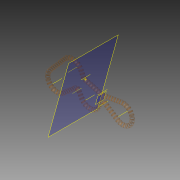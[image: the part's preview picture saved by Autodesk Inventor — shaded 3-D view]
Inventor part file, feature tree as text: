
AUTODESK INVENTOR PART (.ipt)
format: ipt  version: 2014 SP1 (Build 180222100, 222)  size: 463,360 bytes
history: native  units: mm (DEFAULTED — no unit token found)
features: other x96, extrude x86, sketch x2, plane x1, pattern_linear x1
ambient origin geometry x8: Origin, YZ Plane, XZ Plane, XY Plane, X Axis, Y Axis, Z Axis, Center Point
bodies: Body1 (feature_tree), Body2 (feature_tree), Body3 (feature_tree), Body4 (feature_tree), Body5 (feature_tree), Body6 (feature_tree), Body7 (feature_tree), Body8 (feature_tree), Body9 (feature_tree), Body10 (feature_tree), Body11 (feature_tree), Body12 (feature_tree), Body13 (feature_tree), Body14 (feature_tree), Body15 (feature_tree), Body16 (feature_tree), Body17 (feature_tree), Body18 (feature_tree), Body19 (feature_tree), Body20 (feature_tree), Body21 (feature_tree), Body22 (feature_tree), Body23 (feature_tree), Body24 (feature_tree), Body25 (feature_tree), Body26 (feature_tree), Body27 (feature_tree), Body28 (feature_tree), Body29 (feature_tree), Body30 (feature_tree), Body31 (feature_tree), Body32 (feature_tree), Body33 (feature_tree), Body34 (feature_tree), Body35 (feature_tree), Body36 (feature_tree), Body37 (feature_tree), Body38 (feature_tree), Body39 (feature_tree), Body40 (feature_tree), Body41 (feature_tree), Body42 (feature_tree), Body43 (feature_tree), Body44 (feature_tree), Body45 (feature_tree), Body46 (feature_tree), Body47 (feature_tree), Body48 (feature_tree), Body49 (feature_tree), Body50 (feature_tree), Body51 (feature_tree), Body52 (feature_tree), Body53 (feature_tree), Body54 (feature_tree), Body55 (feature_tree), Body56 (feature_tree), Body57 (feature_tree), Body58 (feature_tree), Body59 (feature_tree), Body60 (feature_tree), Body61 (feature_tree), Body62 (feature_tree), Body63 (feature_tree), Body64 (feature_tree), Body65 (feature_tree), Body66 (feature_tree), Body67 (feature_tree), Body68 (feature_tree), Body69 (feature_tree), Body70 (feature_tree), Body71 (feature_tree), Body72 (feature_tree), Body73 (feature_tree), Body74 (feature_tree), Body75 (feature_tree), Body76 (feature_tree), Body77 (feature_tree), Body78 (feature_tree), Body79 (feature_tree), Body80 (feature_tree), Body81 (feature_tree), Body82 (feature_tree), Body83 (feature_tree), Body84 (feature_tree), Body85 (feature_tree), Body86 (feature_tree)
feature tree (186):
  sketch  "Sketch Path"  dims[d7=0.0mm d8=0.0mm d9=0.0mm d10=0.0mm d11=0.0mm d12=0.0mm d13=0.0mm d14=0.0mm d15=0.0mm d16=5.08mm d17=0.0mm d18=860.0mm]
  other  "Cross Section Plane"
  other  "Work Axis1"
  other  "Work Axis2"
  other  "Work Axis3"
  other  "Work Axis4"
  other  "Work Axis5"
  other  "Work Axis6"
  other  "Work Axis7"
  other  "Work Axis8"
  other  "Work Point1"
  plane  "Work Plane2"
  pattern_linear  "Rectangular Pattern1"  Spacing1=5.08mm  [1 undecoded]
  sketch  "Sketch3"  dims[d0=0.0mm]
  other  "Srf1"
  other  "Srf2"
  other  "Srf3"
  other  "Srf4"
  other  "Srf5"
  other  "Srf6"
  other  "Srf7"
  other  "Srf8"
  other  "Srf9"
  other  "Srf10"
  other  "Srf11"
  other  "Srf12"
  other  "Srf13"
  other  "Srf14"
  other  "Srf15"
  other  "Srf16"
  other  "Srf17"
  other  "Srf18"
  other  "Srf19"
  other  "Srf20"
  other  "Srf21"
  other  "Srf22"
  other  "Srf23"
  other  "Srf24"
  other  "Srf25"
  other  "Srf26"
  other  "Srf27"
  other  "Srf28"
  other  "Srf29"
  other  "Srf30"
  other  "Srf31"
  other  "Srf32"
  other  "Srf33"
  other  "Srf34"
  other  "Srf35"
  other  "Srf36"
  other  "Srf37"
  other  "Srf38"
  other  "Srf39"
  other  "Srf40"
  other  "Srf41"
  other  "Srf42"
  other  "Srf43"
  other  "Srf44"
  other  "Srf45"
  other  "Srf46"
  other  "Srf47"
  other  "Srf48"
  other  "Srf49"
  other  "Srf50"
  other  "Srf51"
  other  "Srf52"
  other  "Srf53"
  other  "Srf54"
  other  "Srf55"
  other  "Srf56"
  other  "Srf57"
  other  "Srf58"
  other  "Srf59"
  other  "Srf60"
  other  "Srf61"
  other  "Srf62"
  other  "Srf63"
  other  "Srf64"
  other  "Srf65"
  other  "Srf66"
  other  "Srf67"
  other  "Srf68"
  other  "Srf69"
  other  "Srf70"
  other  "Srf71"
  other  "Srf72"
  other  "Srf73"
  other  "Srf74"
  other  "Srf75"
  other  "Srf76"
  other  "Srf77"
  other  "Srf78"
  other  "Srf79"
  other  "Srf80"
  other  "Srf81"
  other  "Srf82"
  other  "Srf83"
  other  "Srf84"
  other  "Srf85"
  other  "Srf86"
  extrude  "ExtrusionSrf1"  Depth=860.0mm
  extrude  "ExtrusionSrf2"  [1 undecoded]
  extrude  "ExtrusionSrf3"  [1 undecoded]
  extrude  "ExtrusionSrf4"  [1 undecoded]
  extrude  "ExtrusionSrf5"  [1 undecoded]
  extrude  "ExtrusionSrf6"  [1 undecoded]
  extrude  "ExtrusionSrf7"  [1 undecoded]
  extrude  "ExtrusionSrf8"  [1 undecoded]
  extrude  "ExtrusionSrf9"  [1 undecoded]
  extrude  "ExtrusionSrf10"  [1 undecoded]
  extrude  "ExtrusionSrf11"  [1 undecoded]
  extrude  "ExtrusionSrf12"  [1 undecoded]
  extrude  "ExtrusionSrf13"  [1 undecoded]
  extrude  "ExtrusionSrf14"  [1 undecoded]
  extrude  "ExtrusionSrf15"  [1 undecoded]
  extrude  "ExtrusionSrf16"  [1 undecoded]
  extrude  "ExtrusionSrf17"  [1 undecoded]
  extrude  "ExtrusionSrf18"  [1 undecoded]
  extrude  "ExtrusionSrf19"  [1 undecoded]
  extrude  "ExtrusionSrf20"  [1 undecoded]
  extrude  "ExtrusionSrf21"  [1 undecoded]
  extrude  "ExtrusionSrf22"  [1 undecoded]
  extrude  "ExtrusionSrf23"  [1 undecoded]
  extrude  "ExtrusionSrf24"  [1 undecoded]
  extrude  "ExtrusionSrf25"  [1 undecoded]
  extrude  "ExtrusionSrf26"  [1 undecoded]
  extrude  "ExtrusionSrf27"  [1 undecoded]
  extrude  "ExtrusionSrf28"  [1 undecoded]
  extrude  "ExtrusionSrf29"  [1 undecoded]
  extrude  "ExtrusionSrf30"  [1 undecoded]
  extrude  "ExtrusionSrf31"  [1 undecoded]
  extrude  "ExtrusionSrf32"  [1 undecoded]
  extrude  "ExtrusionSrf33"  [1 undecoded]
  extrude  "ExtrusionSrf34"  [1 undecoded]
  extrude  "ExtrusionSrf35"  [1 undecoded]
  extrude  "ExtrusionSrf36"  [1 undecoded]
  extrude  "ExtrusionSrf37"  [1 undecoded]
  extrude  "ExtrusionSrf38"  [1 undecoded]
  extrude  "ExtrusionSrf39"  [1 undecoded]
  extrude  "ExtrusionSrf40"  [1 undecoded]
  extrude  "ExtrusionSrf41"  [1 undecoded]
  extrude  "ExtrusionSrf42"  [1 undecoded]
  extrude  "ExtrusionSrf43"  [1 undecoded]
  extrude  "ExtrusionSrf44"  [1 undecoded]
  extrude  "ExtrusionSrf45"  [1 undecoded]
  extrude  "ExtrusionSrf46"  [1 undecoded]
  extrude  "ExtrusionSrf47"  [1 undecoded]
  extrude  "ExtrusionSrf48"  [1 undecoded]
  extrude  "ExtrusionSrf49"  [1 undecoded]
  extrude  "ExtrusionSrf50"  [1 undecoded]
  extrude  "ExtrusionSrf51"  [1 undecoded]
  extrude  "ExtrusionSrf52"  [1 undecoded]
  extrude  "ExtrusionSrf53"  [1 undecoded]
  extrude  "ExtrusionSrf54"  [1 undecoded]
  extrude  "ExtrusionSrf55"  [1 undecoded]
  extrude  "ExtrusionSrf56"  [1 undecoded]
  extrude  "ExtrusionSrf57"  [1 undecoded]
  extrude  "ExtrusionSrf58"  [1 undecoded]
  extrude  "ExtrusionSrf59"  [1 undecoded]
  extrude  "ExtrusionSrf60"  [1 undecoded]
  extrude  "ExtrusionSrf61"  [1 undecoded]
  extrude  "ExtrusionSrf62"  [1 undecoded]
  extrude  "ExtrusionSrf63"  [1 undecoded]
  extrude  "ExtrusionSrf64"  [1 undecoded]
  extrude  "ExtrusionSrf65"  [1 undecoded]
  extrude  "ExtrusionSrf66"  [1 undecoded]
  extrude  "ExtrusionSrf67"  [1 undecoded]
  extrude  "ExtrusionSrf68"  [1 undecoded]
  extrude  "ExtrusionSrf69"  [1 undecoded]
  extrude  "ExtrusionSrf70"  [1 undecoded]
  extrude  "ExtrusionSrf71"  [1 undecoded]
  extrude  "ExtrusionSrf72"  [1 undecoded]
  extrude  "ExtrusionSrf73"  [1 undecoded]
  extrude  "ExtrusionSrf74"  [1 undecoded]
  extrude  "ExtrusionSrf75"  [1 undecoded]
  extrude  "ExtrusionSrf76"  [1 undecoded]
  extrude  "ExtrusionSrf77"  [1 undecoded]
  extrude  "ExtrusionSrf78"  [1 undecoded]
  extrude  "ExtrusionSrf79"  [1 undecoded]
  extrude  "ExtrusionSrf80"  [1 undecoded]
  extrude  "ExtrusionSrf81"  [1 undecoded]
  extrude  "ExtrusionSrf82"  [1 undecoded]
  extrude  "ExtrusionSrf83"  [1 undecoded]
  extrude  "ExtrusionSrf84"  [1 undecoded]
  extrude  "ExtrusionSrf85"  [1 undecoded]
  extrude  "ExtrusionSrf86"  [1 undecoded]
note: 86 required parameter values undecoded (feature->parameter linkage not recoverable at this tier; creation-order binding heuristic only, values carry confidence <= 0.55)
